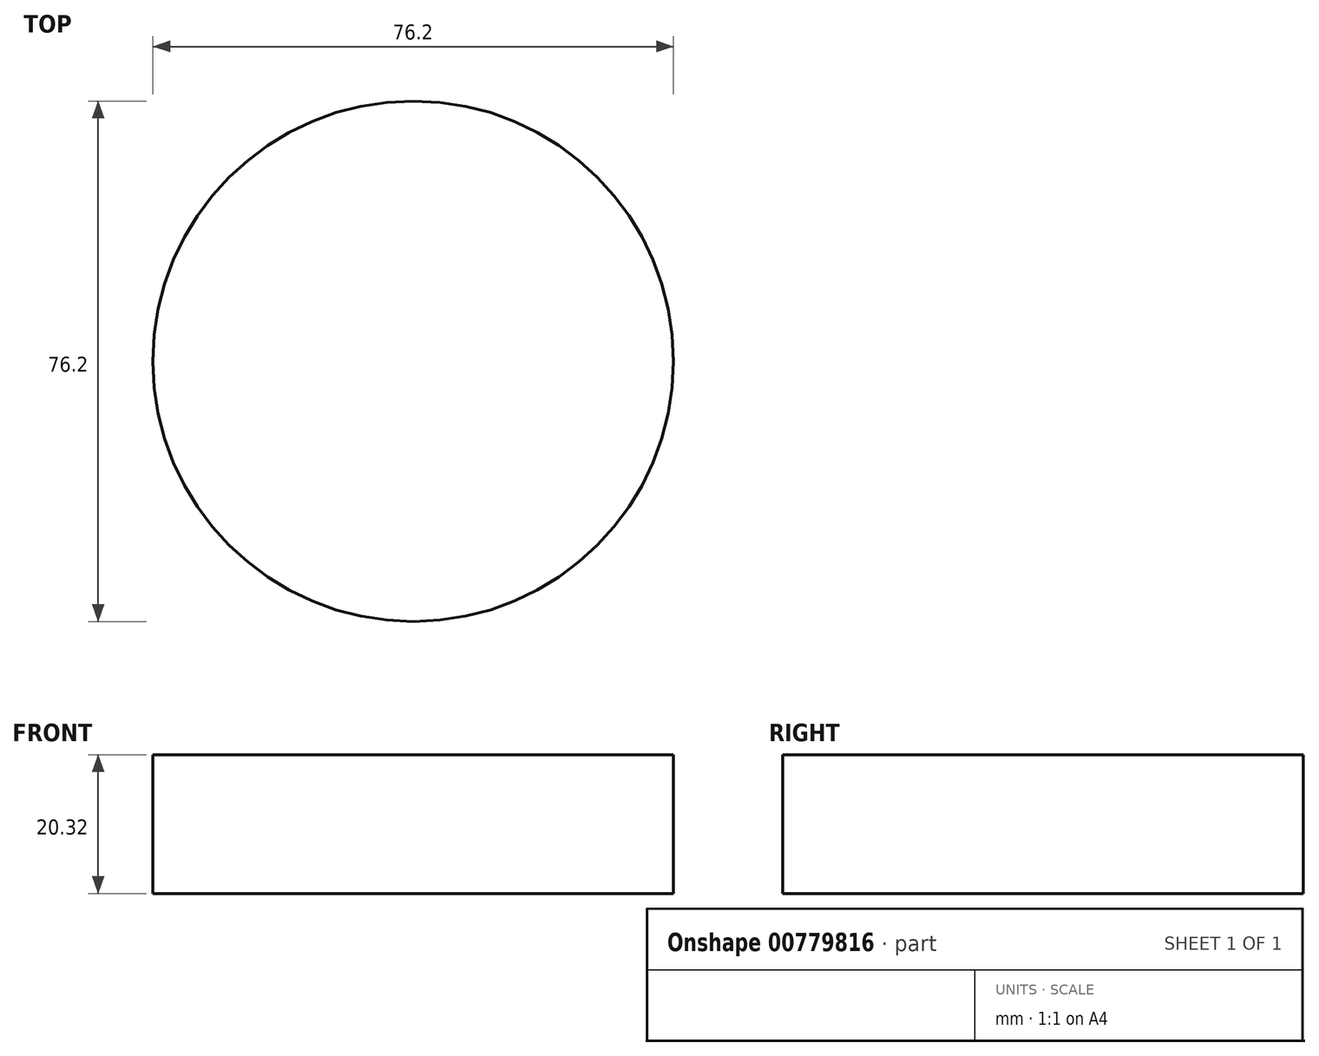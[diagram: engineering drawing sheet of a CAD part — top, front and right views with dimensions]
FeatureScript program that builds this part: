
annotation { "Feature Type Name" : "Feature", "Feature Type Description" : "" }
export const myFeature = defineFeature(function(context is Context, id is Id, definition is map)
    precondition{}
    {
        {
            var Q0;
            Q0=qCreatedBy(makeId("Top.planeOp"),FACE);
            var sketch = newSketch(context, id + "F0", { "sketchPlane" : qUnion([Q0])});
            skCircle(sketch, "E0", {"center": v(0, 0) * mm, "radius": 38.1 * mm});
            skSolve(sketch);
        }
        {
            var Q0;
            Q0=makeQuery(id+"F0.imprint","IMPRINT",FACE,{"disambiguationData":[TD([[makeQuery(id+"F0.imprint","IMPRINT",EDGE,{"derivedFrom":sQuery(id+"F0.wireOp",EDGE,"E0")}),1.0]])]});
            extrude(context, id + "F1", {"entities" : qUnion([Q0]), "depth" : 20.32 * mm, "offsetDistance" : 25.4 * mm});
        }
    });
